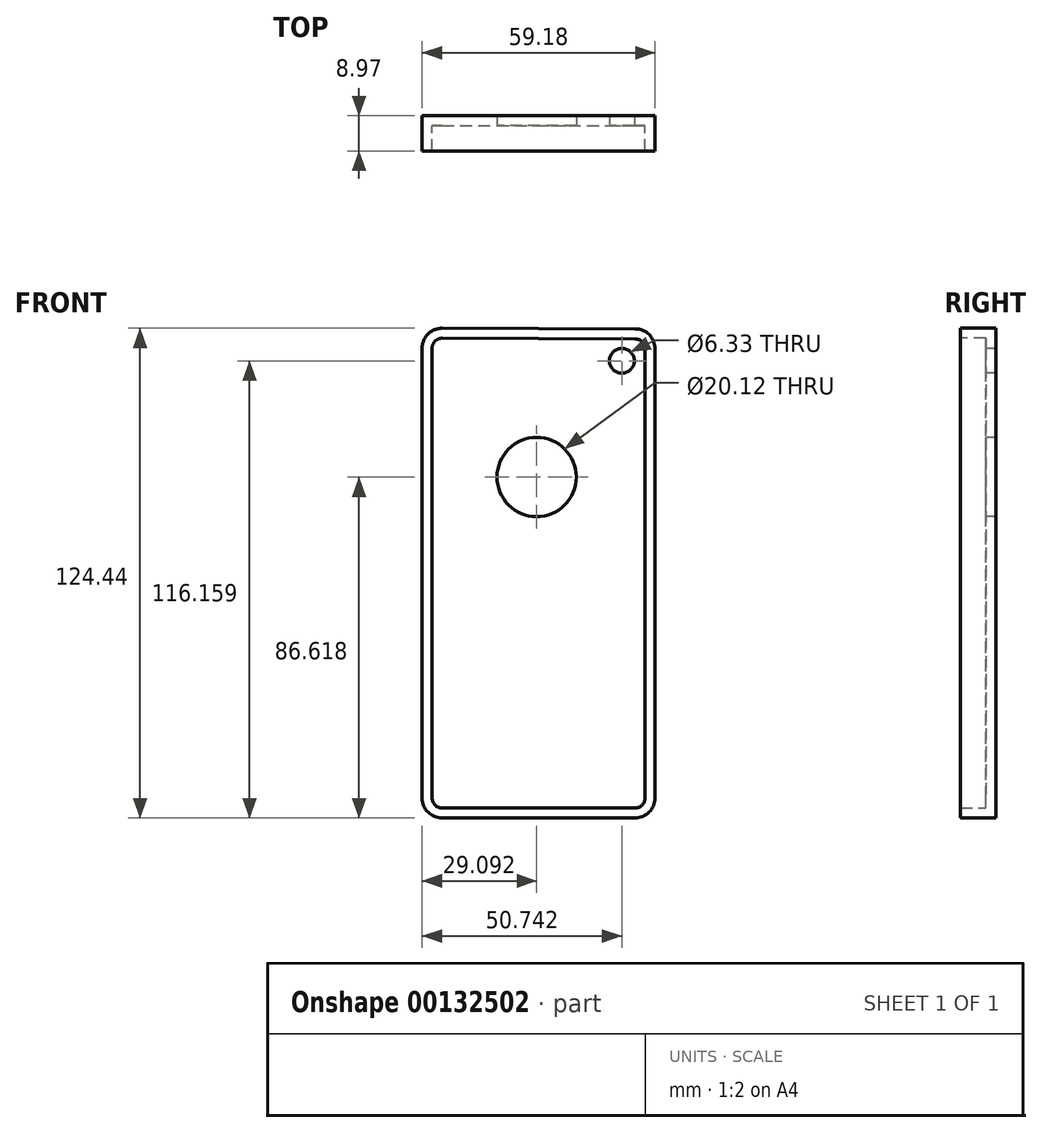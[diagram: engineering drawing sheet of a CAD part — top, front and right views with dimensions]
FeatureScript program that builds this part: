
annotation { "Feature Type Name" : "Feature", "Feature Type Description" : "" }
export const myFeature = defineFeature(function(context is Context, id is Id, definition is map)
    precondition{}
    {
        {
            var Q0;
            Q0=qCreatedBy(makeId("Front.planeOp"),FACE);
            var sketch = newSketch(context, id + "F0", { "sketchPlane" : qUnion([Q0])});
            skLineSegment(sketch, "E0", {"start": v(-75.8, -49.5) * mm, "end": v(-16.61, -49.5) * mm});
            skLineSegment(sketch, "E1", {"start": v(-16.61, -49.5) * mm, "end": v(-16.61, 74.76) * mm});
            skLineSegment(sketch, "E2", {"start": v(-75.8, 74.96) * mm, "end": v(-75.8, -49.5) * mm});
            skLineSegment(sketch, "E3", {"start": v(-75.8, 74.96) * mm, "end": v(-16.61, 74.76) * mm});
            skSolve(sketch);
        }
        {
            var Q0;
            Q0 = qSketchRegion(id + "F0", true);
            extrude(context, id + "F1", {"entities" : qUnion([Q0]), "depth" : 8.97 * mm});
        }
        {
            var Q0;
            Q0=makeQuery(id+"F1.opExtrude","SWEPT_EDGE",EDGE,{"disambiguationData":[OSD([sQuery(id+"F0.wireOp",EDGE,"E1"),sQuery(id+"F0.wireOp",EDGE,"E3")])]});
            var Q1;
            Q1=makeQuery(id+"F1.opExtrude","SWEPT_EDGE",EDGE,{"disambiguationData":[OSD([sQuery(id+"F0.wireOp",EDGE,"E0"),sQuery(id+"F0.wireOp",EDGE,"E1")])]});
            fillet(context, id + "F2", {"entities" : qUnion([Q0, Q1]), "radius" : 5.08 * mm, "tangentPropagation" : true, "allowEdgeOverflow" : false});
        }
        {
            var Q0;
            Q0=makeQuery(id+"F1.opExtrude","SWEPT_EDGE",EDGE,{"disambiguationData":[OSD([sQuery(id+"F0.wireOp",EDGE,"E2"),sQuery(id+"F0.wireOp",EDGE,"E3")])]});
            var Q1;
            Q1=makeQuery(id+"F1.opExtrude","SWEPT_EDGE",EDGE,{"disambiguationData":[OSD([sQuery(id+"F0.wireOp",EDGE,"E0"),sQuery(id+"F0.wireOp",EDGE,"E2")])]});
            fillet(context, id + "F3", {"entities" : qUnion([Q0, Q1]), "radius" : 5.08 * mm, "tangentPropagation" : true, "allowEdgeOverflow" : false});
        }
        {
            var Q0;
            Q0=makeQuery(id+"F1.opExtrude","CAP_FACE",FACE,{"disambiguationData":[OSD([sQuery(id+"F0.wireOp",EDGE,"E0"),sQuery(id+"F0.wireOp",EDGE,"E1"),sQuery(id+"F0.wireOp",EDGE,"E2"),sQuery(id+"F0.wireOp",EDGE,"E3")])],"isStart":false});
            var sketch = newSketch(context, id + "F4", { "sketchPlane" : qUnion([Q0])});
            skCircle(sketch, "E4", {"center": v(-25.05, 66.66) * mm, "radius": 3.17 * mm});
            skSolve(sketch);
        }
        {
            var Q0;
            Q0=makeQuery(id+"F4.imprint","IMPRINT",FACE,{"disambiguationData":[TD([[makeQuery(id+"F4.imprint","IMPRINT",EDGE,{"derivedFrom":sQuery(id+"F4.wireOp",EDGE,"E4")}),1.0]])]});
            extrude(context, id + "F5", {"entities" : qUnion([Q0]), "operationType" : NewBodyOperationType.REMOVE, "oppositeDirection" : true, "depth" : 25.4 * mm});
        }
        {
            var Q0;
            Q0=makeQuery(id+"F1.opExtrude","CAP_FACE",FACE,{"disambiguationData":[OSD([sQuery(id+"F0.wireOp",EDGE,"E0"),sQuery(id+"F0.wireOp",EDGE,"E1"),sQuery(id+"F0.wireOp",EDGE,"E2"),sQuery(id+"F0.wireOp",EDGE,"E3")])],"isStart":false});
            var sketch = newSketch(context, id + "F6", { "sketchPlane" : qUnion([Q0])});
            skCircle(sketch, "E5", {"center": v(-46.7, 37.12) * mm, "radius": 10.06 * mm});
            skSolve(sketch);
        }
        {
            var Q0;
            Q0=makeQuery(id+"F6.imprint","IMPRINT",FACE,{"disambiguationData":[TD([[makeQuery(id+"F6.imprint","IMPRINT",EDGE,{"derivedFrom":sQuery(id+"F6.wireOp",EDGE,"E5")}),1.0]])]});
            extrude(context, id + "F7", {"entities" : qUnion([Q0]), "operationType" : NewBodyOperationType.REMOVE, "oppositeDirection" : true, "depth" : 25.4 * mm});
        }
        {
            var Q0;
            Q0=makeQuery(id+"F1.opExtrude","CAP_FACE",FACE,{"disambiguationData":[OSD([sQuery(id+"F0.wireOp",EDGE,"E0"),sQuery(id+"F0.wireOp",EDGE,"E1"),sQuery(id+"F0.wireOp",EDGE,"E2"),sQuery(id+"F0.wireOp",EDGE,"E3")])],"isStart":false});
            var Q1;
            Q1=makeQuery(id+"F7.boolean.opBoolean","COPY",FACE,{"derivedFrom":makeQuery(id+"F7.opExtrude","SWEPT_FACE",FACE,{"disambiguationData":[OSD([sQuery(id+"F6.wireOp",EDGE,"E5")])]})});
            var Q2;
            Q2=makeQuery(id+"F5.boolean.opBoolean","COPY",FACE,{"derivedFrom":makeQuery(id+"F5.opExtrude","SWEPT_FACE",FACE,{"disambiguationData":[OSD([sQuery(id+"F4.wireOp",EDGE,"E4")])]})});
            shell(context, id + "F8", {"entities" : qUnion([Q0, Q1, Q2]), "thickness" : 2.54 * mm});
        }
    });
